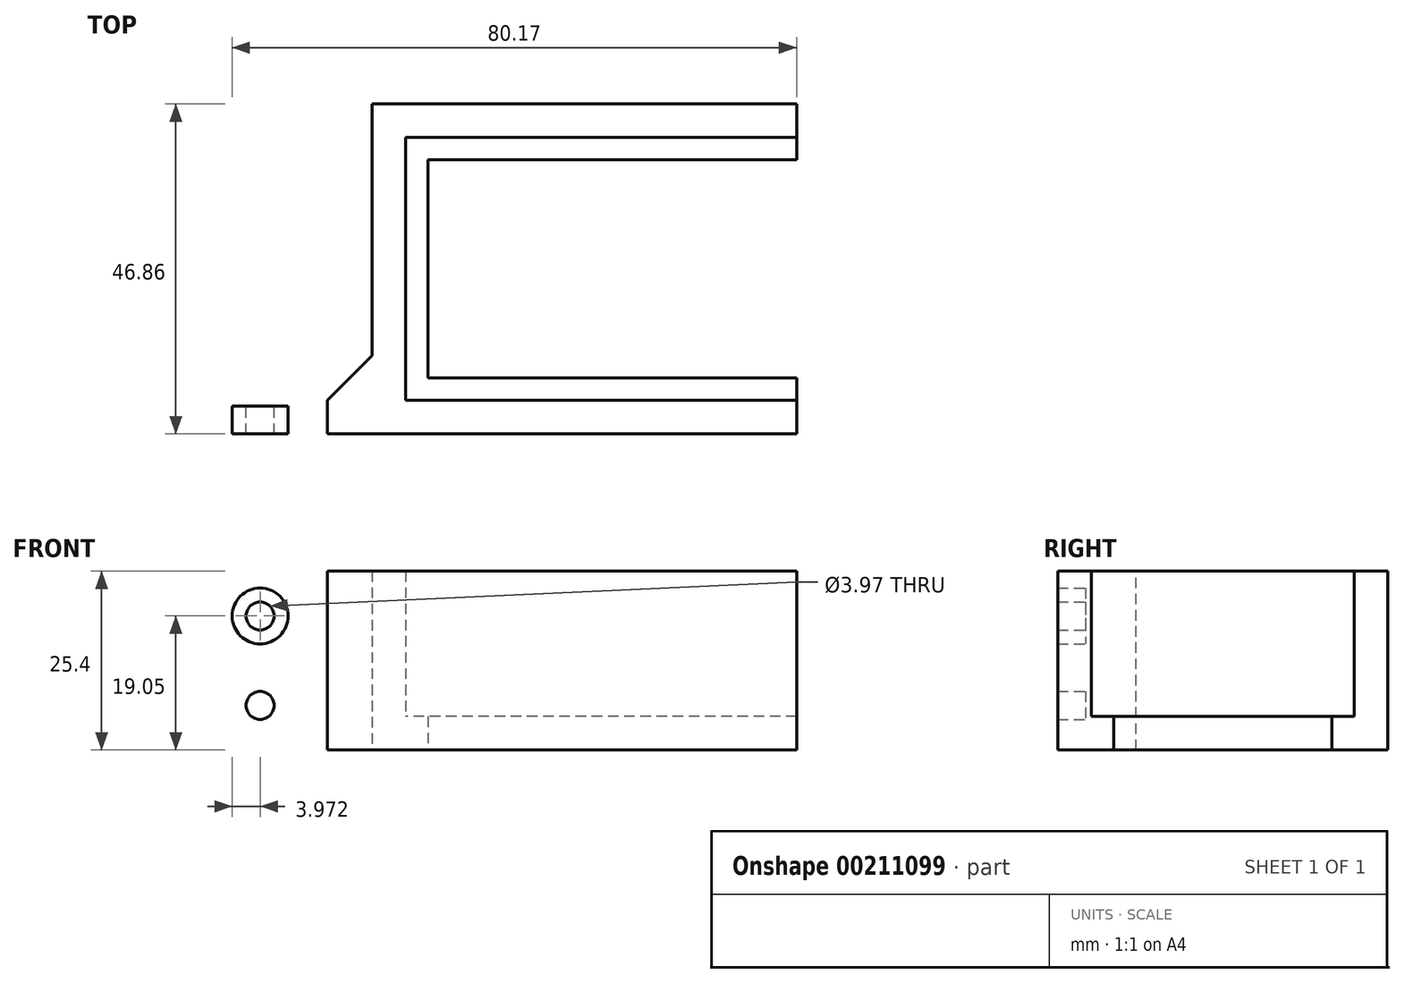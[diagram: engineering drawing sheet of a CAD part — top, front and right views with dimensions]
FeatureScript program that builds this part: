
annotation { "Feature Type Name" : "Feature", "Feature Type Description" : "" }
export const myFeature = defineFeature(function(context is Context, id is Id, definition is map)
    precondition{}
    {
        {
            var Q0;
            Q0=qCreatedBy(makeId("Top.planeOp"),FACE);
            var sketch = newSketch(context, id + "F0", { "sketchPlane" : qUnion([Q0])});
            skLineSegment(sketch, "E0.bottom", {"start": v(25.4, 18.67) * mm, "end": v(-25.4, 18.67) * mm});
            skLineSegment(sketch, "E0.top", {"start": v(25.4, -18.67) * mm, "end": v(-25.4, -18.67) * mm});
            skLineSegment(sketch, "E0.left", {"start": v(25.4, 18.67) * mm, "end": v(25.4, -18.67) * mm});
            skLineSegment(sketch, "E0.right", {"start": v(-25.4, 18.67) * mm, "end": v(-25.4, -18.67) * mm});
            skPoint(sketch, "E0.middle", {"position": v(0, 0) * mm});
            skLineSegment(sketch, "E1.0", {"start": v(30.16, 23.43) * mm, "end": v(-30.16, 23.43) * mm});
            skLineSegment(sketch, "E1.1", {"start": v(30.16, 23.43) * mm, "end": v(30.16, -23.43) * mm});
            skLineSegment(sketch, "E1.2", {"start": v(30.16, -23.43) * mm, "end": v(-30.16, -23.43) * mm});
            skLineSegment(sketch, "E1.3", {"start": v(-30.16, 23.43) * mm, "end": v(-30.16, -23.43) * mm});
            skLineSegment(sketch, "E2", {"start": v(25.4, -18.67) * mm, "end": v(30.16, -18.67) * mm});
            skLineSegment(sketch, "E3", {"start": v(25.4, 18.67) * mm, "end": v(30.16, 18.67) * mm});
            skLineSegment(sketch, "E4", {"start": v(-25.4, -18.67) * mm, "end": v(-55.56, -18.67) * mm});
            skLineSegment(sketch, "E5", {"start": v(-55.56, -18.67) * mm, "end": v(-55.56, -23.43) * mm});
            skLineSegment(sketch, "E6", {"start": v(-55.56, -23.43) * mm, "end": v(-30.16, -23.43) * mm});
            skLineSegment(sketch, "E7.0", {"start": v(30.16, -15.5) * mm, "end": v(-22.22, -15.5) * mm});
            skLineSegment(sketch, "E7.1", {"start": v(-22.23, 15.5) * mm, "end": v(-22.22, -15.5) * mm});
            skLineSegment(sketch, "E7.2", {"start": v(30.16, 15.5) * mm, "end": v(-22.23, 15.5) * mm});
            skSolve(sketch);
        }
        {
            var Q0;
            {var subQ0=sQuery(id+"F0.wireOp",EDGE,"E3");Q0=makeQuery(id+"F0.imprint","IMPRINT",FACE,{"disambiguationData":[TD([[makeQuery(id+"F0.imprint","IMPRINT",EDGE,{"derivedFrom":subQ0}),-1.0]])]});}
            var Q1;
            {var subQ0=sQuery(id+"F0.wireOp",EDGE,"E2");Q1=makeQuery(id+"F0.imprint","IMPRINT",FACE,{"disambiguationData":[TD([[makeQuery(id+"F0.imprint","IMPRINT",EDGE,{"derivedFrom":subQ0}),1.0]])]});}
            var Q2;
            {var subQ4=sQuery(id+"F0.wireOp",EDGE,"E5");Q2=makeQuery(id+"F0.imprint","IMPRINT",FACE,{"disambiguationData":[TD([[makeQuery(id+"F0.imprint","IMPRINT",EDGE,{"derivedFrom":subQ4}),1.0]])]});}
            var Q3;
            {var subQ6=sQuery(id+"F0.wireOp",EDGE,"E0.top");Q3=makeQuery(id+"F0.imprint","IMPRINT",FACE,{"disambiguationData":[TD([[makeQuery(id+"F0.imprint","IMPRINT",EDGE,{"derivedFrom":subQ6}),1.0]])]});}
            var Q4;
            Q4=makeQuery(id+"F0.imprint","IMPRINT",FACE,{"disambiguationData":[TD([[makeQuery(id+"F0.imprint","IMPRINT",EDGE,{"derivedFrom":sQuery(id+"F0.wireOp",EDGE,"E0.bottom")}),-1.0]])]});
            var Q5;
            {var subQ4=sQuery(id+"F0.wireOp",EDGE,"E0.bottom");Q5=makeQuery(id+"F0.imprint","IMPRINT",FACE,{"disambiguationData":[TD([[makeQuery(id+"F0.imprint","IMPRINT",EDGE,{"derivedFrom":subQ4}),1.0]])]});}
            extrude(context, id + "F1", {"entities" : qUnion([Q0, Q1, Q2, Q3, Q4, Q5]), "depth" : 4.76 * mm});
        }
        {
            var Q0;
            {var subQ4=sQuery(id+"F0.wireOp",EDGE,"E5");Q0=makeQuery(id+"F0.imprint","IMPRINT",FACE,{"disambiguationData":[TD([[makeQuery(id+"F0.imprint","IMPRINT",EDGE,{"derivedFrom":subQ4}),1.0]])]});}
            var Q1;
            {var subQ4=sQuery(id+"F0.wireOp",EDGE,"E0.top");Q1=makeQuery(id+"F0.imprint","IMPRINT",FACE,{"disambiguationData":[TD([[makeQuery(id+"F0.imprint","IMPRINT",EDGE,{"derivedFrom":subQ4}),1.0]])]});}
            var Q2;
            Q2=makeQuery(id+"F0.imprint","IMPRINT",FACE,{"disambiguationData":[TD([[makeQuery(id+"F0.imprint","IMPRINT",EDGE,{"derivedFrom":sQuery(id+"F0.wireOp",EDGE,"E0.bottom")}),-1.0]])]});
            extrude(context, id + "F2", {"entities" : qUnion([Q0, Q1, Q2]), "operationType" : NewBodyOperationType.ADD, "depth" : 25.4 * mm});
        }
        {
            var Q0;
            {var subQ0=sQuery(id+"F0.wireOp",EDGE,"E4");var subQ1=sQuery(id+"F0.wireOp",EDGE,"E1.3");Q0=makeQuery(id+"F2.boolean.opBoolean","MERGE",EDGE,{"derivedFrom":[makeQuery(id+"F1.opExtrude","SWEPT_EDGE",EDGE,{"disambiguationData":[OSD([subQ1,subQ0])]}),makeQuery(id+"F2.opExtrude","SWEPT_EDGE",EDGE,{"disambiguationData":[OSD([subQ1,subQ0])]})]});}
            chamfer(context, id + "F3", {"entities" : qUnion([Q0]), "width" : 6.35 * mm, "tangentPropagation" : true});
        }
        {
            var Q0;
            {var subQ0=sQuery(id+"F0.wireOp",EDGE,"E4");Q0=makeQuery(id+"F2.boolean.opBoolean","MERGE",FACE,{"derivedFrom":[makeQuery(id+"F1.opExtrude","SWEPT_FACE",FACE,{"disambiguationData":[OSD([subQ0])]}),makeQuery(id+"F2.opExtrude","SWEPT_FACE",FACE,{"disambiguationData":[OSD([subQ0])]})]});}
            var sketch = newSketch(context, id + "F4", { "sketchPlane" : qUnion([Q0])});
            skCircle(sketch, "E8", {"center": v(46.04, 19.05) * mm, "radius": 1.98 * mm});
            skPoint(sketch, "E8.centerSnap0", {"position": v(46.04, 25.4) * mm});
            skCircle(sketch, "E9.MirrorC", {"center": v(46.04, 6.35) * mm, "radius": 1.98 * mm});
            skCircle(sketch, "E10", {"center": v(46.04, 19.05) * mm, "radius": 3.97 * mm});
            skCircle(sketch, "E11.MirrorC", {"center": v(46.04, 6.35) * mm, "radius": 3.97 * mm});
            skSolve(sketch);
        }
        {
            var Q0;
            Q0=makeQuery(id+"F4.imprint","IMPRINT",FACE,{"disambiguationData":[TD([[makeQuery(id+"F4.imprint","IMPRINT",EDGE,{"derivedFrom":sQuery(id+"F4.wireOp",EDGE,"E9.MirrorC")}),1.0]])]});
            var Q1;
            Q1=makeQuery(id+"F4.imprint","IMPRINT",FACE,{"disambiguationData":[TD([[makeQuery(id+"F4.imprint","IMPRINT",EDGE,{"derivedFrom":sQuery(id+"F4.wireOp",EDGE,"E8")}),-1.0]])]});
            extrude(context, id + "F5", {"entities" : qUnion([Q0, Q1]), "operationType" : NewBodyOperationType.REMOVE, "oppositeDirection" : true, "depth" : 0.8 * mm});
        }
        {
            var Q0;
            {var subQ0=sQuery(id+"F0.wireOp",EDGE,"E4");Q0=makeQuery(id+"F5.boolean.opBoolean","SPLIT",FACE,{"disambiguationData":[TD([makeQuery(id+"F5.opExtrude","SWEPT_FACE",FACE,{"disambiguationData":[OSD([sQuery(id+"F4.wireOp",EDGE,"E9.MirrorC")])]})])],"derivedFrom":makeQuery(id+"F2.boolean.opBoolean","MERGE",FACE,{"derivedFrom":[makeQuery(id+"F1.opExtrude","SWEPT_FACE",FACE,{"disambiguationData":[OSD([subQ0])]}),makeQuery(id+"F2.opExtrude","SWEPT_FACE",FACE,{"disambiguationData":[OSD([subQ0])]})]})});}
            var Q1;
            {var subQ0=sQuery(id+"F0.wireOp",EDGE,"E4");Q1=makeQuery(id+"F5.boolean.opBoolean","SPLIT",FACE,{"disambiguationData":[TD([makeQuery(id+"F5.opExtrude","SWEPT_FACE",FACE,{"disambiguationData":[OSD([sQuery(id+"F4.wireOp",EDGE,"E8")])]})])],"derivedFrom":makeQuery(id+"F2.boolean.opBoolean","MERGE",FACE,{"derivedFrom":[makeQuery(id+"F1.opExtrude","SWEPT_FACE",FACE,{"disambiguationData":[OSD([subQ0])]}),makeQuery(id+"F2.opExtrude","SWEPT_FACE",FACE,{"disambiguationData":[OSD([subQ0])]})]})});}
            var Q2;
            {var subQ0=sQuery(id+"F0.wireOp",EDGE,"E6");var subQ1=sQuery(id+"F0.wireOp",EDGE,"E1.2");Q2=makeQuery(id+"F2.boolean.opBoolean","MERGE",FACE,{"derivedFrom":[makeQuery(id+"F1.opExtrude","SWEPT_FACE",FACE,{"disambiguationData":[OSD([subQ1,subQ0])]}),makeQuery(id+"F2.opExtrude","SWEPT_FACE",FACE,{"disambiguationData":[OSD([subQ1,subQ0])]})]});}
            extrude(context, id + "F6", {"entities" : qUnion([Q0, Q1]), "operationType" : NewBodyOperationType.REMOVE, "endBound" : BoundingType.UP_TO_SURFACE, "oppositeDirection" : true, "endBoundEntityFace" : qUnion([Q2]), "depth" : 25.4 * mm});
        }
    });
